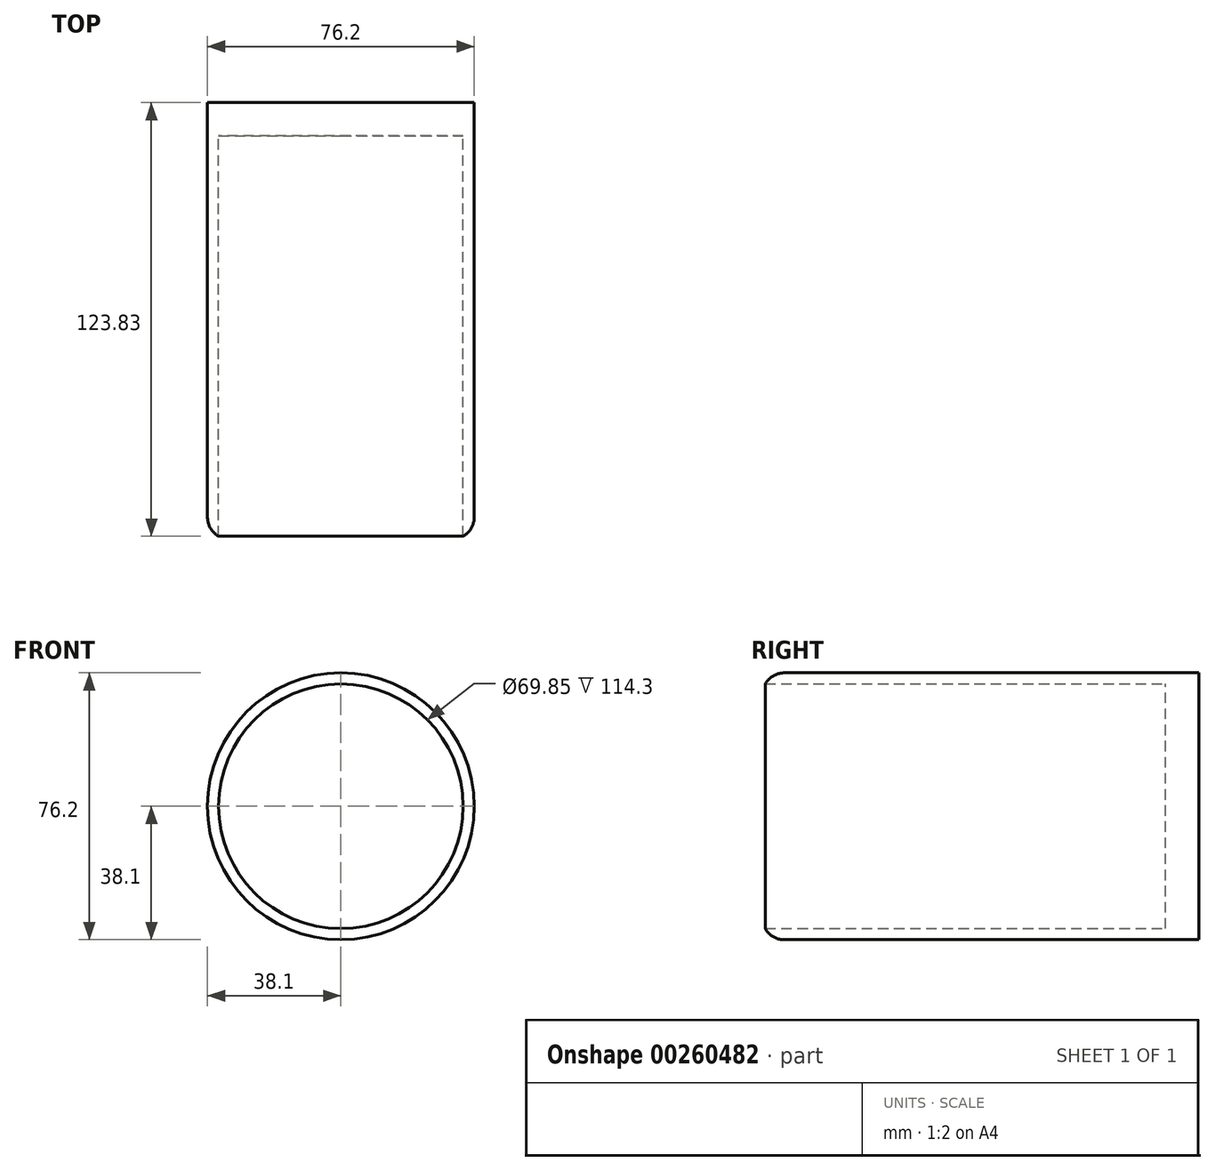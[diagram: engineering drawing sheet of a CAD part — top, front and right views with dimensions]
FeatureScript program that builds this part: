
annotation { "Feature Type Name" : "Feature", "Feature Type Description" : "" }
export const myFeature = defineFeature(function(context is Context, id is Id, definition is map)
    precondition{}
    {
        {
            var Q0;
            Q0=qCreatedBy(makeId("Front.planeOp"),FACE);
            var sketch = newSketch(context, id + "F0", { "sketchPlane" : qUnion([Q0])});
            skCircle(sketch, "E0", {"center": v(0, 0) * mm, "radius": 38.1 * mm});
            skCircle(sketch, "E1", {"center": v(0, 0) * mm, "radius": 34.93 * mm});
            skSolve(sketch);
        }
        {
            var Q0;
            Q0=makeQuery(id+"F0.imprint","IMPRINT",FACE,{"disambiguationData":[TD([[makeQuery(id+"F0.imprint","IMPRINT",EDGE,{"derivedFrom":sQuery(id+"F0.wireOp",EDGE,"E1")}),1.0]])]});
            extrude(context, id + "F1", {"entities" : qUnion([Q0]), "depth" : 9.52 * mm});
        }
        {
            var Q0;
            Q0 = qSketchRegion(id + "F0", true);
            extrude(context, id + "F2", {"entities" : qUnion([Q0]), "operationType" : NewBodyOperationType.ADD, "depth" : 123.82 * mm});
        }
        {
            var Q0;
            Q0=makeQuery(id+"F2.opExtrude","CAP_EDGE",EDGE,{"disambiguationData":[OSD([sQuery(id+"F0.wireOp",EDGE,"E0")])],"isStart":false});
            fillet(context, id + "F3", {"entities" : qUnion([Q0]), "radius" : 6.35 * mm, "tangentPropagation" : true, "allowEdgeOverflow" : false});
        }
    });
